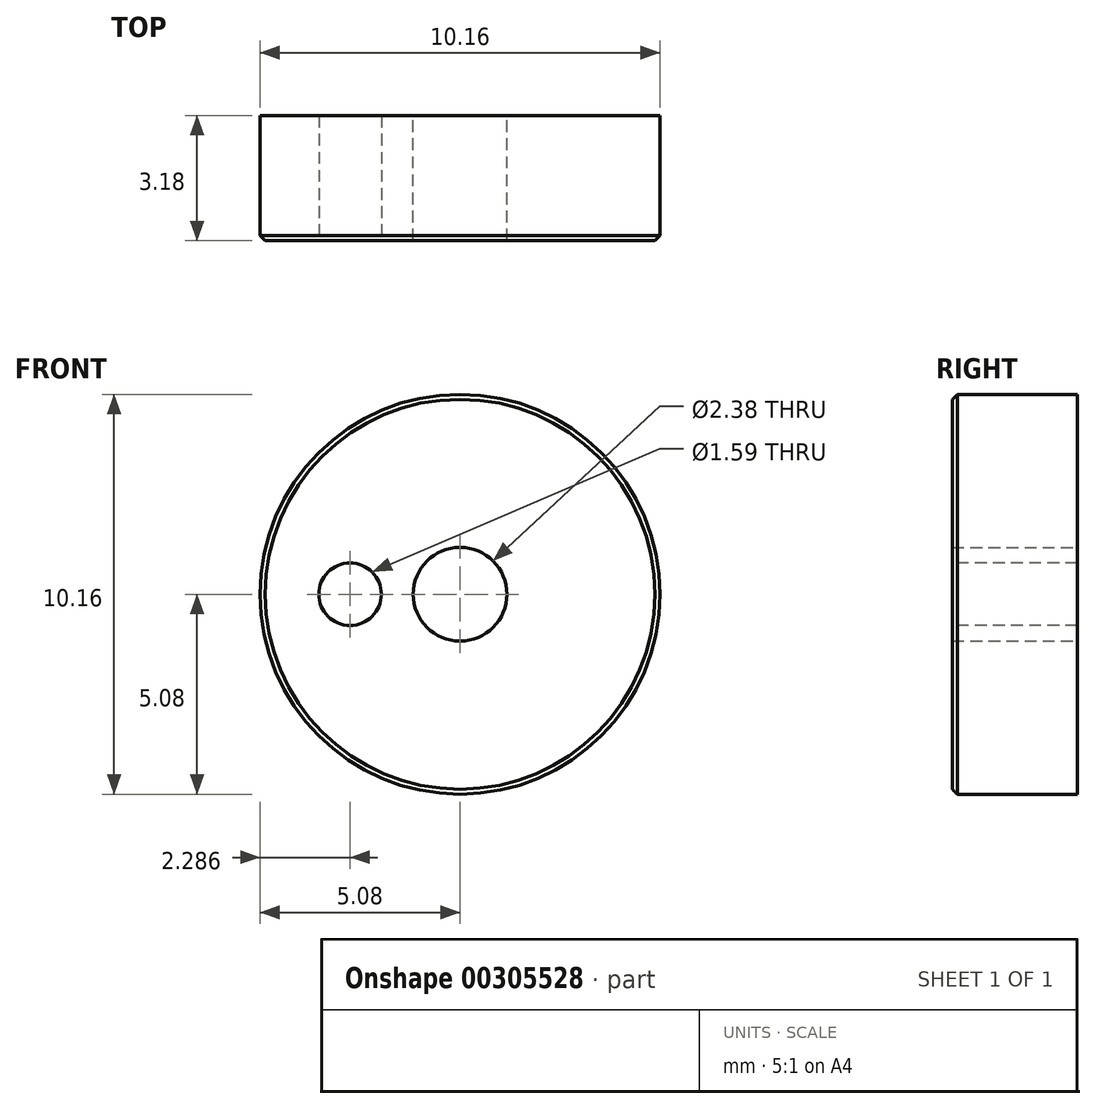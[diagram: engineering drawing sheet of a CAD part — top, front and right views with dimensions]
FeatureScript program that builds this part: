
annotation { "Feature Type Name" : "Feature", "Feature Type Description" : "" }
export const myFeature = defineFeature(function(context is Context, id is Id, definition is map)
    precondition{}
    {
        {
            var Q0;
            Q0=qCreatedBy(makeId("Front.planeOp"),FACE);
            var sketch = newSketch(context, id + "F0", { "sketchPlane" : qUnion([Q0])});
            skCircle(sketch, "E0", {"center": v(0, 0) * mm, "radius": 5.08 * mm});
            skCircle(sketch, "E1", {"center": v(0, 0) * mm, "radius": 1.2 * mm});
            skSolve(sketch);
        }
        {
            var Q0;
            Q0=makeQuery(id+"F0.imprint","IMPRINT",FACE,{"disambiguationData":[TD([[makeQuery(id+"F0.imprint","IMPRINT",EDGE,{"derivedFrom":sQuery(id+"F0.wireOp",EDGE,"E0")}),1.0]])]});
            extrude(context, id + "F1", {"entities" : qUnion([Q0]), "depth" : 3.17 * mm});
        }
        {
            var Q0;
            Q0=makeQuery(id+"F1.opExtrude","CAP_EDGE",EDGE,{"disambiguationData":[OSD([sQuery(id+"F0.wireOp",EDGE,"E0")])],"isStart":false});
            chamfer(context, id + "F2", {"entities" : qUnion([Q0]), "width" : 0.13 * mm, "tangentPropagation" : true});
        }
        {
            var Q0;
            Q0=qCreatedBy(makeId("Front.planeOp"),FACE);
            var sketch = newSketch(context, id + "F3", { "sketchPlane" : qUnion([Q0])});
            skLineSegment(sketch, "E2", {"start": v(0, 0) * mm, "end": v(-2.8, 0) * mm});
            skCircle(sketch, "E3", {"center": v(-2.8, 0) * mm, "radius": 0.8 * mm});
            skSolve(sketch);
        }
        {
            var Q0;
            Q0 = qSketchRegion(id + "F3", true);
            extrude(context, id + "F4", {"entities" : qUnion([Q0]), "operationType" : NewBodyOperationType.REMOVE, "oppositeDirection" : true, "depth" : 25.4 * mm, "hasSecondDirection" : true, "secondDirectionOppositeDirection" : false, "secondDirectionDepth" : 25.4 * mm});
        }
    });
